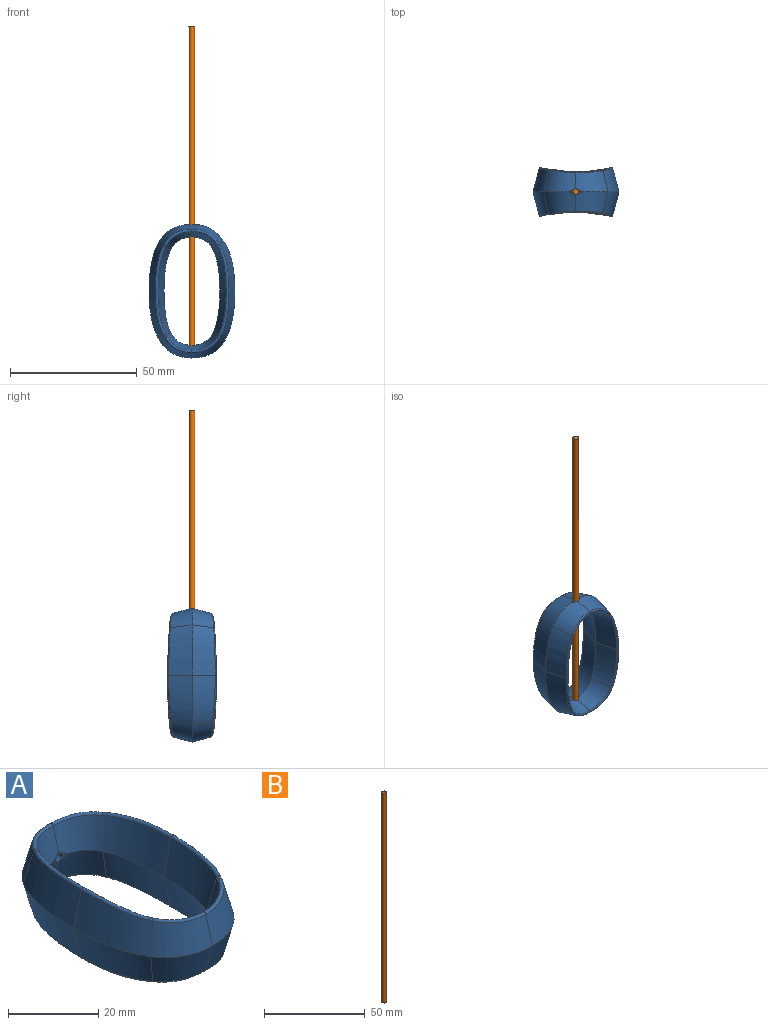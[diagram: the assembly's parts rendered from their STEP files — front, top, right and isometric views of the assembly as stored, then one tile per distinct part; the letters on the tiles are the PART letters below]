
ASSEMBLY  parts=2 mates=1
PART A: 59 faces, bbox 33.9x52.8x30.5 mm
  f0: bspline ~18.17x15.24mm, area 157.3mm2, adj f1,f15,f25,f28
  f1: bspline ~17.39x9.17mm, area 159.7mm2, adj f0,f2,f27,f29
  f2: bspline ~15.24x12mm, area 96.4mm2, adj f1,f3,f24,f26,f30,f58
  f3: bspline ~15.24x12.08mm, area 94.7mm2, adj f2,f4,f20,f22,f31,f58
  f4: bspline ~17.32x9.31mm, area 158.4mm2, adj f3,f5,f18,f32
  f5: bspline ~18.07x15.24mm, area 161.5mm2, adj f4,f6,f16,f33
  f6: bspline ~10.51x8.68mm, area 97.6mm2, adj f5,f15,f17,f19,f34,f57
  f7: bspline ~19.86x9.31mm, area 186.7mm2, adj f8,f14,f16,f17,f35
  f8: bspline ~19.6x15.24mm, area 181.4mm2, adj f7,f9,f18,f20,f36
  f9: bspline ~12.68x8.2mm, area 113.8mm2, adj f8,f10,f22,f37,f58
  f10: bspline ~15.24x12.73mm, area 115.1mm2, adj f9,f11,f24,f38,f58
  f11: bspline ~19.88x15.24mm, area 184.4mm2, adj f10,f12,f26,f27,f39
  f12: bspline ~19.71x15.24mm, area 179.9mm2, adj f11,f13,f23,f25,f40
  f13: bspline ~15.24x12.59mm, area 112.6mm2, adj f12,f14,f21,f41
  f14: bspline ~15.24x12.82mm, area 116.5mm2, adj f7,f13,f19,f42
  f15: bspline ~15.24x12.01mm, area 93.1mm2, adj f0,f6,f21,f23,f43,f57
  f16: bspline ~19.58x4.28mm, area 23.9mm2, adj f5,f7,f17,f18
  f17: bspline ~4.48x3.07mm, area 1.3mm2, adj f6,f7,f16,f19
  f18: bspline ~19.26x4.41mm, area 23.8mm2, adj f4,f8,f16,f20
  f19: bspline ~11.32x6.84mm, area 16.6mm2, adj f6,f14,f17,f21
  f20: bspline ~4.26x3.02mm, area 1.1mm2, adj f3,f8,f18,f22
  f21: bspline ~11.14x6.66mm, area 16.4mm2, adj f13,f15,f19,f23
  f22: bspline ~11.66x6.71mm, area 16.6mm2, adj f3,f9,f20,f24
  f23: bspline ~4.2x2.99mm, area 1.1mm2, adj f12,f15,f21,f25
  f24: bspline ~11.71x6.76mm, area 16.4mm2, adj f2,f10,f22,f26
  f25: bspline ~18.88x4.41mm, area 24mm2, adj f0,f12,f23,f27
  f26: bspline ~4.43x3.06mm, area 1.3mm2, adj f2,f11,f24,f27
  f27: bspline ~19.16x4.27mm, area 24mm2, adj f1,f11,f25,f26
  f28: bspline ~18.17x15.24mm, area 157.3mm2, adj f0,f29,f43,f53
  f29: bspline ~17.39x9.17mm, area 159.7mm2, adj f1,f28,f30,f55
  f30: bspline ~15.24x12mm, area 96.4mm2, adj f2,f29,f31,f52,f54,f58
  f31: bspline ~15.24x12.08mm, area 94.7mm2, adj f3,f30,f32,f48,f50,f58
  f32: bspline ~17.32x9.31mm, area 158.4mm2, adj f4,f31,f33,f46
  f33: bspline ~18.07x15.24mm, area 161.5mm2, adj f5,f32,f34,f44
  f34: bspline ~10.51x8.68mm, area 97.6mm2, adj f6,f33,f43,f45,f47,f57
  f35: bspline ~19.86x9.31mm, area 186.7mm2, adj f7,f36,f42,f44,f45
  f36: bspline ~19.6x15.24mm, area 181.4mm2, adj f8,f35,f37,f46,f48
  f37: bspline ~12.68x8.2mm, area 113.8mm2, adj f9,f36,f38,f50,f58
  f38: bspline ~15.24x12.73mm, area 115.1mm2, adj f10,f37,f39,f52,f58
  f39: bspline ~19.88x15.24mm, area 184.4mm2, adj f11,f38,f40,f54,f55
  f40: bspline ~19.71x15.24mm, area 179.9mm2, adj f12,f39,f41,f51,f53
  f41: bspline ~15.24x12.59mm, area 112.6mm2, adj f13,f40,f42,f49
  f42: bspline ~15.24x12.82mm, area 116.5mm2, adj f14,f35,f41,f47
  f43: bspline ~15.24x12.01mm, area 92.2mm2, adj f15,f28,f34,f49,f51,f57
  f44: bspline ~19.58x4.28mm, area 23.9mm2, adj f33,f35,f45,f46
  f45: bspline ~4.48x3.07mm, area 1.3mm2, adj f34,f35,f44,f47
  f46: bspline ~19.26x4.41mm, area 23.8mm2, adj f32,f36,f44,f48
  f47: bspline ~11.32x6.84mm, area 16.6mm2, adj f34,f42,f45,f49
  f48: bspline ~4.26x3.02mm, area 1.1mm2, adj f31,f36,f46,f50
  f49: bspline ~11.14x6.66mm, area 16.4mm2, adj f41,f43,f47,f51
  f50: bspline ~11.66x6.71mm, area 16.6mm2, adj f31,f37,f48,f52
  f51: bspline ~4.2x2.99mm, area 1.1mm2, adj f40,f43,f49,f53
  f52: bspline ~11.71x6.76mm, area 16.4mm2, adj f30,f38,f50,f54
  f53: bspline ~18.88x4.41mm, area 24mm2, adj f28,f40,f51,f55
  f54: bspline ~4.43x3.06mm, area 1.3mm2, adj f30,f39,f52,f55
  f55: bspline ~19.16x4.27mm, area 24mm2, adj f29,f39,f53,f54
  f56: plane 2.23x2.23mm, normal (0,1,0), area 3.9mm2, adj f57
  f57: cylinder r=1.11mm len=2.23mm, axis (0,-1,0), area 5.4mm2, adj f6,f15,f34,f43,f56
  f58: cylinder r=1.11mm len=5.08mm, axis (0,-1,0), area 33.4mm2, adj f2,f3,f9,f10,f30,f31,f37,f38
PART B: 3 faces, bbox 2.2x2.2x127 mm
  f0: cylinder r=1.11mm len=127mm, axis (0,0,-1), area 889.6mm2, adj f1,f2
  f1: plane 2.23x2.23mm, normal (0,0,1), area 3.9mm2, adj f0
  f2: plane 2.23x2.23mm, normal (0,0,-1), area 3.9mm2, adj f0
PLACE A rot(axis=(1,0,0),90deg) t=(-11.15,-12.14,23.2)mm
PLACE B t=(-18.33,-12.14,-2.2)mm
MATE planar B.f0 <-> A.f57  axis (0,0,-1) through (-18.33,-12.14,-2.2)mm
